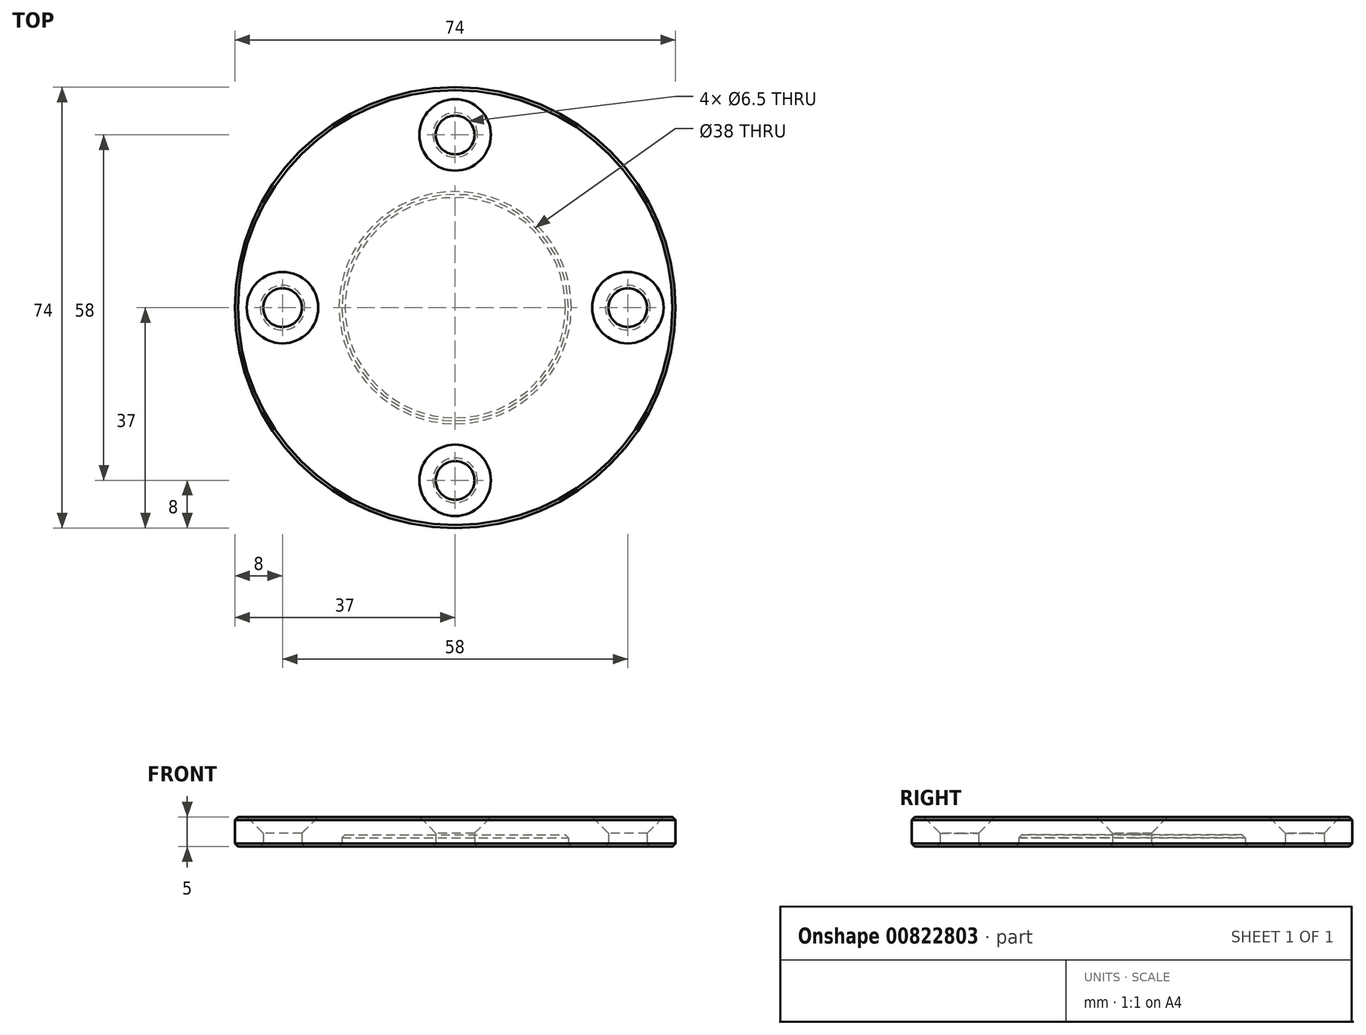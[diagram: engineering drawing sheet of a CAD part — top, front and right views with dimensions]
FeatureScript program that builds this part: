
annotation { "Feature Type Name" : "Feature", "Feature Type Description" : "" }
export const myFeature = defineFeature(function(context is Context, id is Id, definition is map)
    precondition{}
    {
        {
            var Q0;
            Q0=qCreatedBy(makeId("Top.planeOp"),FACE);
            var sketch = newSketch(context, id + "F0", { "sketchPlane" : qUnion([Q0])});
            skCircle(sketch, "E0", {"center": v(0, 0) * mm, "radius": 16 * mm, "construction": true});
            skCircle(sketch, "E1", {"center": v(0, 0) * mm, "radius": 29 * mm, "construction": true});
            skCircle(sketch, "E2", {"center": v(0, 0) * mm, "radius": 37 * mm});
            skLineSegment(sketch, "E3", {"start": v(0, -37) * mm, "end": v(0, 37) * mm, "construction": true});
            skLineSegment(sketch, "E4", {"start": v(0, 37) * mm, "end": v(37, 0) * mm, "construction": true});
            skLineSegment(sketch, "E5", {"start": v(37, 0) * mm, "end": v(-37, 0) * mm, "construction": true});
            skCircle(sketch, "E6", {"center": v(0, 29) * mm, "radius": 3.25 * mm});
            skCircle(sketch, "E7", {"center": v(-29, 0) * mm, "radius": 3.25 * mm});
            skCircle(sketch, "E8", {"center": v(0, -29) * mm, "radius": 3.25 * mm});
            skCircle(sketch, "E9", {"center": v(29, 0) * mm, "radius": 3.25 * mm});
            skSolve(sketch);
        }
        {
            var Q0;
            Q0=qSketchRegion(id+"F0",true);
            extrude(context, id + "F1", {"entities" : qUnion([Q0]), "depth" : 5 * mm, "offsetDistance" : 25 * mm});
        }
        {
            var Q0;
            Q0=makeQuery(id+"F1.opExtrude","CAP_EDGE",EDGE,{"disambiguationData":[OSD([sQuery(id+"F0.wireOp",EDGE,"E8")])],"isStart":false});
            var Q1;
            Q1=makeQuery(id+"F1.opExtrude","CAP_EDGE",EDGE,{"disambiguationData":[OSD([sQuery(id+"F0.wireOp",EDGE,"E7")])],"isStart":false});
            var Q2;
            Q2=makeQuery(id+"F1.opExtrude","CAP_EDGE",EDGE,{"disambiguationData":[OSD([sQuery(id+"F0.wireOp",EDGE,"E6")])],"isStart":false});
            var Q3;
            Q3=makeQuery(id+"F1.opExtrude","CAP_EDGE",EDGE,{"disambiguationData":[OSD([sQuery(id+"F0.wireOp",EDGE,"E9")])],"isStart":false});
            chamfer(context, id + "F2", {"entities" : qUnion([Q0, Q1, Q2, Q3]), "width" : 2.75 * mm, "tangentPropagation" : true});
        }
        {
            var Q0;
            Q0=makeQuery(id+"F1.opExtrude","SWEPT_FACE",FACE,{"disambiguationData":[OSD([sQuery(id+"F0.wireOp",EDGE,"E2")])]});
            var Q1;
            Q1=makeQuery(id+"F1.opExtrude","CAP_EDGE",EDGE,{"disambiguationData":[OSD([sQuery(id+"F0.wireOp",EDGE,"E8")])],"isStart":true});
            var Q2;
            Q2=makeQuery(id+"F1.opExtrude","CAP_EDGE",EDGE,{"disambiguationData":[OSD([sQuery(id+"F0.wireOp",EDGE,"E7")])],"isStart":true});
            var Q3;
            Q3=makeQuery(id+"F1.opExtrude","CAP_EDGE",EDGE,{"disambiguationData":[OSD([sQuery(id+"F0.wireOp",EDGE,"E6")])],"isStart":true});
            var Q4;
            Q4=makeQuery(id+"F1.opExtrude","CAP_EDGE",EDGE,{"disambiguationData":[OSD([sQuery(id+"F0.wireOp",EDGE,"E9")])],"isStart":true});
            chamfer(context, id + "F3", {"entities" : qUnion([Q0, Q1, Q2, Q3, Q4]), "width" : 0.5 * mm, "tangentPropagation" : true});
        }
        {
            var Q0;
            Q0=makeQuery(id+"F1.opExtrude","CAP_FACE",FACE,{"disambiguationData":[OSD([sQuery(id+"F0.wireOp",EDGE,"E2"),sQuery(id+"F0.wireOp",EDGE,"E6"),sQuery(id+"F0.wireOp",EDGE,"E7"),sQuery(id+"F0.wireOp",EDGE,"E8"),sQuery(id+"F0.wireOp",EDGE,"E9")])],"isStart":true});
            var sketch = newSketch(context, id + "F4", { "sketchPlane" : qUnion([Q0])});
            skCircle(sketch, "E10", {"center": v(0, 0) * mm, "radius": 19 * mm});
            skSolve(sketch);
        }
        {
            var Q0;
            Q0=makeQuery(id+"F4.imprint","IMPRINT",FACE,{"disambiguationData":[TD([[makeQuery(id+"F4.imprint","IMPRINT",EDGE,{"derivedFrom":sQuery(id+"F4.wireOp",EDGE,"E10")}),1.0]])]});
            extrude(context, id + "F5", {"entities" : qUnion([Q0]), "operationType" : NewBodyOperationType.REMOVE, "oppositeDirection" : true, "depth" : 2 * mm, "offsetDistance" : 25 * mm});
        }
        {
            var Q0;
            Q0=makeQuery(id+"F5.boolean.opBoolean","COPY",FACE,{"derivedFrom":makeQuery(id+"F5.opExtrude","SWEPT_FACE",FACE,{"disambiguationData":[OSD([sQuery(id+"F4.wireOp",EDGE,"E10")])]})});
            chamfer(context, id + "F6", {"entities" : qUnion([Q0]), "width" : 0.5 * mm, "tangentPropagation" : true});
        }
    });
